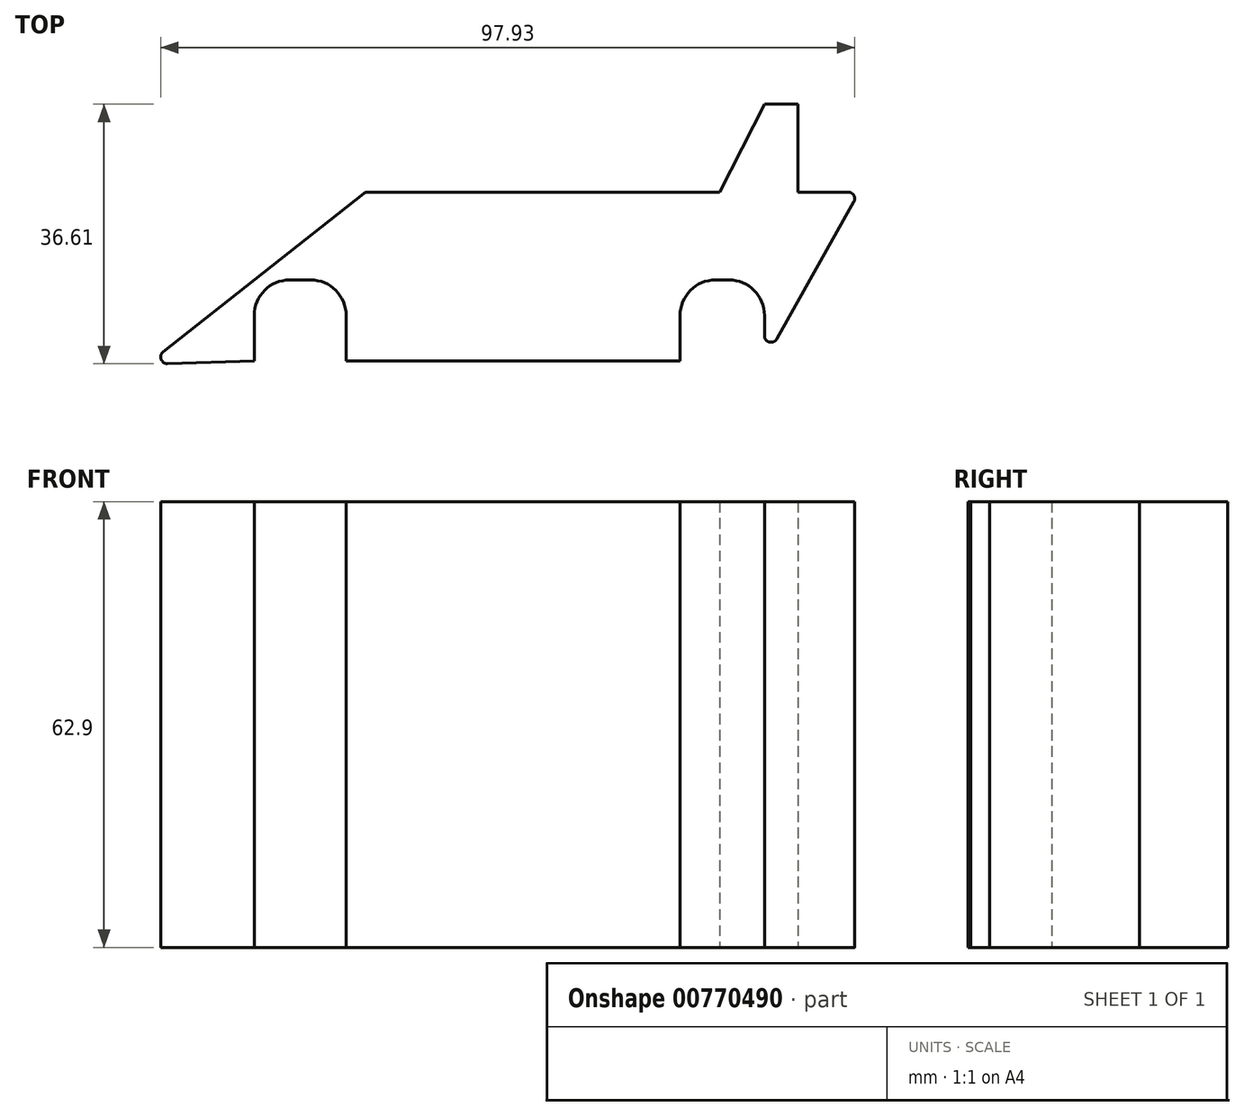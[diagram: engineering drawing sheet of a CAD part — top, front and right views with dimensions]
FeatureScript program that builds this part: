
annotation { "Feature Type Name" : "Feature", "Feature Type Description" : "" }
export const myFeature = defineFeature(function(context is Context, id is Id, definition is map)
    precondition{}
    {
        {
            var Q0;
            Q0=qCreatedBy(makeId("Top.planeOp"),FACE);
            var sketch = newSketch(context, id + "F0", { "sketchPlane" : qUnion([Q0])});
            skLineSegment(sketch, "E0", {"start": v(-48.51, -10.16) * mm, "end": v(-20.22, 12.2) * mm});
            skLineSegment(sketch, "E1", {"start": v(-19.64, 12.4) * mm, "end": v(30.03, 12.4) * mm});
            skLineSegment(sketch, "E2", {"start": v(30.03, 12.4) * mm, "end": v(36.34, 24.8) * mm});
            skLineSegment(sketch, "E3", {"start": v(36.34, 24.8) * mm, "end": v(41.05, 24.8) * mm});
            skLineSegment(sketch, "E4", {"start": v(41.05, 24.8) * mm, "end": v(41.05, 12.4) * mm});
            skLineSegment(sketch, "E5", {"start": v(41.05, 12.4) * mm, "end": v(48.14, 12.4) * mm});
            skLineSegment(sketch, "E6", {"start": v(48.95, 11.02) * mm, "end": v(38.07, -8.32) * mm});
            skLineSegment(sketch, "E7", {"start": v(36.34, -7.87) * mm, "end": v(36.34, -5) * mm});
            skLineSegment(sketch, "E8", {"start": v(31.34, 0) * mm, "end": v(29.43, 0) * mm});
            skLineSegment(sketch, "E9", {"start": v(24.43, -5) * mm, "end": v(24.43, -11.4) * mm});
            skLineSegment(sketch, "E10", {"start": v(24.43, -11.4) * mm, "end": v(-22.7, -11.4) * mm});
            skLineSegment(sketch, "E11", {"start": v(-22.7, -11.4) * mm, "end": v(-22.7, -5) * mm});
            skLineSegment(sketch, "E12", {"start": v(-27.7, 0) * mm, "end": v(-30.66, 0) * mm});
            skLineSegment(sketch, "E13", {"start": v(-35.66, -5) * mm, "end": v(-35.66, -11.4) * mm});
            skLineSegment(sketch, "E14", {"start": v(-35.66, -11.4) * mm, "end": v(-47.9, -11.81) * mm});
            skPoint(sketch, "E15.visualSharp", {"position": v(-35.66, 0) * mm});
            skArc(sketch, "E15.filletArc", {"start": v(-30.66, 0) * mm, "mid": v(-34.2, -1.46) * mm, "end": v(-35.66, -5) * mm});
            skPoint(sketch, "E16.visualSharp", {"position": v(-22.7, 0) * mm});
            skArc(sketch, "E16.filletArc", {"start": v(-22.7, -5) * mm, "mid": v(-24.16, -1.46) * mm, "end": v(-27.7, 0) * mm});
            skPoint(sketch, "E17.visualSharp", {"position": v(24.43, 0) * mm});
            skArc(sketch, "E17.filletArc", {"start": v(29.43, 0) * mm, "mid": v(25.9, -1.46) * mm, "end": v(24.43, -5) * mm});
            skPoint(sketch, "E18.visualSharp", {"position": v(36.34, 0) * mm});
            skArc(sketch, "E18.filletArc", {"start": v(36.34, -5) * mm, "mid": v(34.87, -1.46) * mm, "end": v(31.34, 0) * mm});
            skPoint(sketch, "E19.visualSharp", {"position": v(36.34, -11.4) * mm});
            skArc(sketch, "E19.filletArc", {"start": v(36.34, -7.87) * mm, "mid": v(37.03, -8.76) * mm, "end": v(38.07, -8.32) * mm});
            skPoint(sketch, "E20.visualSharp", {"position": v(49.73, 12.4) * mm});
            skArc(sketch, "E20.filletArc", {"start": v(48.95, 11.02) * mm, "mid": v(48.94, 11.94) * mm, "end": v(48.14, 12.4) * mm});
            skPoint(sketch, "E21.visualSharp", {"position": v(-50.72, -11.9) * mm});
            skArc(sketch, "E21.filletArc", {"start": v(-48.51, -10.16) * mm, "mid": v(-48.8, -11.2) * mm, "end": v(-47.9, -11.81) * mm});
            skPoint(sketch, "E22.visualSharp", {"position": v(-19.97, 12.4) * mm});
            skArc(sketch, "E22.filletArc", {"start": v(-19.64, 12.4) * mm, "mid": v(-19.95, 12.35) * mm, "end": v(-20.22, 12.2) * mm});
            skSolve(sketch);
        }
        {
            var Q0;
            Q0=makeQuery(id+"F0.imprint","IMPRINT",FACE,{"disambiguationData":[TD([[makeQuery(id+"F0.imprint","IMPRINT",EDGE,{"derivedFrom":sQuery(id+"F0.wireOp",EDGE,"E0")}),-1.0]])]});
            extrude(context, id + "F1", {"entities" : qUnion([Q0]), "depth" : 62.9 * mm, "offsetDistance" : 25 * mm});
        }
    });
